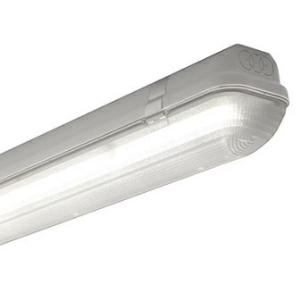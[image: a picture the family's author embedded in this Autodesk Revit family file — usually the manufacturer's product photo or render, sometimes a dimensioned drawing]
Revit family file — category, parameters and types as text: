
# Revit family: 3f_filippi_-_3f_linda_hq_3f_filippi_-_58875_-_3f_linda_led_1x24w-940_dali_l1270
name_source: partatom
category: Lighting Fixtures
units: mm (PartAtom-declared; Revit-internal decimal feet)

## family parameters
Cut with Voids When Loaded = No
Host = Face
Light Source = No
Part Type = Normal
Room Calculation Point = No
Round Connector Dimension = Use Diameter
Shared = No

## types (1)
- 3F Filippi - 3F Linda HQ (1 x LED, 3150 lm, 28 W, 4000 K)
    Apparent Load = 28 VA
    Approval mark = CE
    CIE Flux Codes = 44 77 94 97 100
    Color Rendering = 90
    Color Temperature = 4000 K
    Control Gear = Electronic transformer
    Default Elevation = 1800 mm
    Description = ILLUMINOTECHNICAL
Luminous efficiency 100% (DLOR 97%, ULOR 3%).
Initial luminous flux of the luminaire 3150 lm.
Controlled symmetric distribution.
Installation Interdistance Transv.D = 1.77 x hu - Long.D = 1.17 x hu.
Tabular UGR (CIE 117 - 4H-8H; S=0.25H; 70/50/20): RUG 21.1 - 22.
Beam angle: 109° - 64°.
Luminous efficacy 113 lm/W.
Lifetime (L93/B10): 30000 h. (tq+25°C)
Lifetime (L90/B10): 50000 h. (tq+25°C)
Lifetime (L85/B10): 80000 h. (tq+25°C)
Lifetime (L80/B10): 100000 h. (tq+25°C)
Lifetime (L85/B10): 50000 h. (tq+35°C)
Sudden decreased luminous flux after 50000 hours: 0% (C0).
Photobiological safety in compliance with IEC/TR 62778: RG0 risk exempt, (IEC 62471).
In compliance with IEC/EN 62722-2-1 - IEC/EN 62717 standards.

SOURCE
Linear LED module 24W/940.
Energy efficiency class (UE 2019/2020 - UE 2019/2015): E.
CIE 13.3 Colour rendering index: CRI >90 (R9 >50%).
IES TM-30 Fidelity Index: Rf = 92 Rg = 101.
CCT nominal colour temperature 4000 K.
Colour initial tolerance (MacAdam): SDCM 3.

MECHANICAL
Self-extinguishing V2 polycarbonate housing, injection moulded, RAL 7035 grey.
Ecologic anti-aging injected sealing gasket.
Diffuser in self-extinguishing V2 polycarbonate, photo-engraved interior, UV stabilised, injection moulded with smooth outer surface, tamper-proof opening.
Gear-holder reflector in hot-dip galvanised steel, painted with white polyester base.
Snug fit safety snap-lock clips for diffuser mounting in stainless steel, screwdriver opening.
Fixing brackets in stainless steel.
Possibility for technicians to access the interior of the luminaire.
Luminaire with limited surface temperature. - D - (EN 60598-2-24)
Dimensions: 1270x100 mm, height 100 mm. Weight 2.085 kg.
IP66 protection degree.
Mechanical strength to impacts IK10 (20 joule).
Glow-wire test resistance 850°C.

ELECTRICAL
Halogen Free DALI-2 DATI (Parts 251, 252, 253), PUSH-DIM, electronic wiring 230V-50/60Hz, power factor 0.90 at full load, THD <25%, constant output current, SELV, class I, 1 driver, 1 DALI addresse.
Power of the luminaire 28 W.
ENEC - CE.
SAFE FLICKER: PstLM=<1 and SVM=<0.4 (IEC TR 61547-1 and IEC TR 63158), to ensure a more comfortable and safe light.
Luminaire compliant with EN 60598-2-22 for power supply from a centralised emergency system CPSS (Central Power Supply System), not incorporated in the luminaire - high risk areas excluded. The default power and flux are 100% in AC and 15% in DC.
Ambient temperature from -20°C to +35°C.
Temperature class T6 max 85°C.
Relative humidity UR: <85%.

INSTALLATION
Ceiling / Suspended / Wall.
All accessories dedicated to this product are available on the Catalog and on our website www.3F-Filippi.com.

APPLICATIONS
Suitable product for food production plants (HACCP), IFS (Food Version 6), BRC (GSFS Food Version 7).
Dry, dusty indoor environments, subject to occasional water splashes.
Virtually shatterproof polycarbonate compatibly with the fumes / atmospheres that compromise the elasticity of plastic materials.
Not suitable for installation on surfaces subject to important vibrations, exposed to weather conditions, on ropes or poles.
Suitable for illumination of public car parks and parking grounds referred to DIN 67528:2018-04.

LIGHT MANAGEMENT
Recommended minimum setting: 10%.
The luminaire, equipped with (DALI-2 DATI) driver, can be controlled manually with 3F Easy Dim technology or automatically/manually with wired or wireless DALI/D2D control systems.
The D2D driver guarantees interoperability with other devices with the same certification by making the following information available:
Device Data (Part 251), Energy Report (Part 252), Diagnosis & Maintenance (Part 253).
In electrical systems without a regulation system (manual or automatic) and DALI bus, a suitable jumper must be made on the DA-DA terminals of the appliance.

WARNING
Fixture not suitable for cold stores with an ambient temperature <0°C and/or relative humidity >85%.
Luminaire designed for disposal/recycling at end-of-life.
Replaceable (LED only) light source by a professional. Replaceable control gear by a professional.
    Height = 100 mm  [stored 0.328084 ft]
    Lamp = 1 x LED
    Lamp Light Flux = 3150 lm
    Lamp Power = 28 W
    Lamp count = 1
    Length = 1270 mm
    Lifetime = 50000 h
    Luminous efficacy = 113 lm/W
    Manufacturer = 3F Filippi
    ModVariant = No
    Model = 3F Filippi - 58875 - 3F Linda LED 1x24W-940 DALI L1270
    Mounting Place = Ceiling
    Mounting Type = Pendant
    Number of Poles = 1
    OnlyDefault = Yes
    Power Factor = 1
    Product Name = 3F Filippi - 3F Linda HQ
    Product group = pendant luminaire
    ProductGroupID = 9
    Protection Class = Protection class I
    Protection Degree = IP 66
    RLX_Detail_Level = 1
    RLX_Emergency_Light_Flux = 0 lm
    RLX_Emergency_Type = 0
    RLX_Emergency_Type_DB = No
    RlxData = <blob elided: 71293 chars, md5=66cbe186>
    Socket = socket
    Standby Power = 0 W
    System Light Flux = 3150 lm
    System Power = 28 W
    Type Comments = Product without accessories
    Type Image = 3ffilippi_3f_linda_led_1x.jpg
    URL = http://relux.com
    VarID = ---
    Voltage = 0 V
    Weight = 0.00 kg
    Width = 100 mm  [stored 0.328084 ft]

note: [stored X ft] marks values corroborated as IEEE doubles in the binary element streams (Revit-internal decimal feet)

## geometry (parser evidence)
native form markers: Blend x4, Sweep x9
no freeform markers — native parametric forms only
